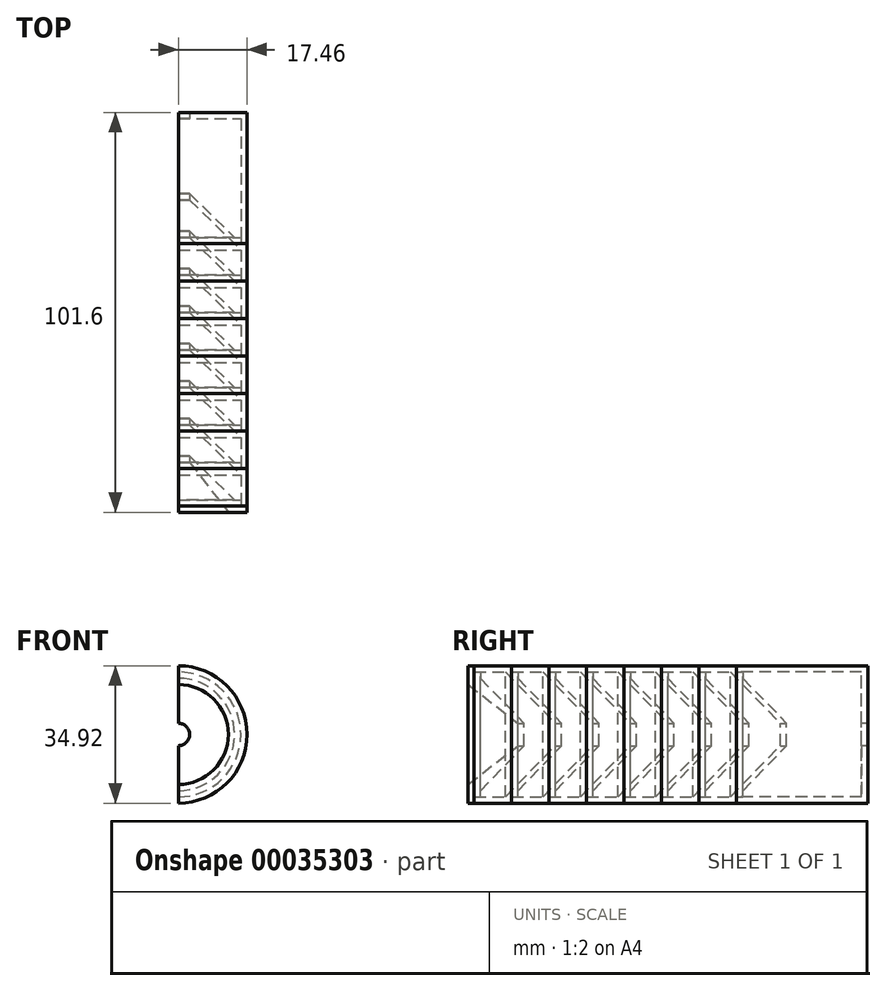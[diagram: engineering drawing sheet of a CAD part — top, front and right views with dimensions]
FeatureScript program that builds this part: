
annotation { "Feature Type Name" : "Feature", "Feature Type Description" : "" }
export const myFeature = defineFeature(function(context is Context, id is Id, definition is map)
    precondition{}
    {
        {
            var Q0;
            Q0=qCreatedBy(makeId("Right.planeOp"),FACE);
            var sketch = newSketch(context, id + "F0", { "sketchPlane" : qUnion([Q0])});
            skLineSegment(sketch, "E0", {"start": v(-16.6, 0) * mm, "end": v(16.6, 0) * mm, "construction": true});
            skLineSegment(sketch, "E1", {"start": v(-11.9, 15.88) * mm, "end": v(-11.9, 17.46) * mm});
            skLineSegment(sketch, "E2", {"start": v(-11.9, 17.46) * mm, "end": v(-21.43, 17.46) * mm});
            skLineSegment(sketch, "E3", {"start": v(-21.43, 17.46) * mm, "end": v(-21.43, 15.88) * mm});
            skLineSegment(sketch, "E4", {"start": v(-21.43, 15.88) * mm, "end": v(-13.5, 15.88) * mm});
            skLineSegment(sketch, "E5", {"start": v(-13.5, 15.88) * mm, "end": v(-0.8, 2.86) * mm});
            skLineSegment(sketch, "E6", {"start": v(-0.8, 2.86) * mm, "end": v(0.8, 2.86) * mm});
            skPoint(sketch, "E7", {"position": v(0, 2.86) * mm});
            skLineSegment(sketch, "E8.bottom", {"start": v(-11.9, 15.88) * mm, "end": v(-10.36, 15.88) * mm});
            skLineSegment(sketch, "E8.top", {"start": v(-11.9, 15.88) * mm, "end": v(-10.36, 15.88) * mm});
            skLineSegment(sketch, "E8.left", {"start": v(-11.9, 15.88) * mm, "end": v(-11.9, 15.88) * mm});
            skLineSegment(sketch, "E8.right", {"start": v(-10.36, 15.88) * mm, "end": v(-10.36, 15.88) * mm});
            skLineSegment(sketch, "E9.top", {"start": v(-10.36, 14.29) * mm, "end": v(-10.36, 14.29) * mm});
            skLineSegment(sketch, "E9.left", {"start": v(-10.36, 15.88) * mm, "end": v(-10.36, 14.29) * mm});
            skLineSegment(sketch, "E9.right", {"start": v(-10.36, 15.88) * mm, "end": v(-10.36, 14.29) * mm});
            skLineSegment(sketch, "E10", {"start": v(-10.36, 14.29) * mm, "end": v(0.8, 2.86) * mm});
            skSolve(sketch);
        }
        {
            var Q0;
            Q0=qCreatedBy(makeId("Right.planeOp"),FACE);
            var sketch = newSketch(context, id + "F1", { "sketchPlane" : qUnion([Q0])});
            skLineSegment(sketch, "E11", {"start": v(0, 0) * mm, "end": v(26.92, 0) * mm, "construction": true});
            skLineSegment(sketch, "E12", {"start": v(-2.38, 15.88) * mm, "end": v(-2.38, 17.46) * mm});
            skLineSegment(sketch, "E13", {"start": v(-2.38, 17.46) * mm, "end": v(-11.9, 17.46) * mm});
            skLineSegment(sketch, "E14", {"start": v(-11.9, 17.46) * mm, "end": v(-11.9, 15.88) * mm});
            skLineSegment(sketch, "E15", {"start": v(-11.9, 15.88) * mm, "end": v(-3.97, 15.88) * mm});
            skLineSegment(sketch, "E16", {"start": v(-3.97, 15.88) * mm, "end": v(8.73, 2.86) * mm});
            skLineSegment(sketch, "E17", {"start": v(8.73, 2.86) * mm, "end": v(10.32, 2.86) * mm});
            skPoint(sketch, "E18", {"position": v(9.52, 2.86) * mm});
            skLineSegment(sketch, "E19", {"start": v(-2.38, 15.88) * mm, "end": v(-0.83, 15.88) * mm});
            skLineSegment(sketch, "E20", {"start": v(-0.83, 15.88) * mm, "end": v(-0.83, 14.29) * mm});
            skLineSegment(sketch, "E21", {"start": v(-0.83, 14.29) * mm, "end": v(10.32, 2.86) * mm});
            skSolve(sketch);
        }
        {
            var Q0;
            Q0=qCreatedBy(makeId("Right.planeOp"),FACE);
            var sketch = newSketch(context, id + "F2", { "sketchPlane" : qUnion([Q0])});
            skLineSegment(sketch, "E22", {"start": v(-1.05, 0) * mm, "end": v(25.87, 0) * mm, "construction": true});
            skLineSegment(sketch, "E23", {"start": v(-21.43, 15.88) * mm, "end": v(-21.43, 17.46) * mm});
            skLineSegment(sketch, "E24", {"start": v(-21.43, 17.46) * mm, "end": v(-30.96, 17.46) * mm});
            skLineSegment(sketch, "E25", {"start": v(-30.96, 17.46) * mm, "end": v(-30.96, 15.88) * mm});
            skLineSegment(sketch, "E26", {"start": v(-30.96, 15.88) * mm, "end": v(-23.02, 15.88) * mm});
            skLineSegment(sketch, "E27", {"start": v(-23.02, 15.88) * mm, "end": v(-10.32, 2.86) * mm});
            skLineSegment(sketch, "E28", {"start": v(-10.32, 2.86) * mm, "end": v(-8.73, 2.86) * mm});
            skPoint(sketch, "E29", {"position": v(-9.53, 2.86) * mm});
            skLineSegment(sketch, "E30", {"start": v(-21.43, 15.88) * mm, "end": v(-19.88, 15.88) * mm});
            skLineSegment(sketch, "E31", {"start": v(-19.88, 15.88) * mm, "end": v(-19.88, 14.29) * mm});
            skLineSegment(sketch, "E32", {"start": v(-19.88, 14.29) * mm, "end": v(-8.73, 2.86) * mm});
            skSolve(sketch);
        }
        {
            var Q0;
            Q0=qCreatedBy(makeId("Right.planeOp"),FACE);
            var sketch = newSketch(context, id + "F3", { "sketchPlane" : qUnion([Q0])});
            skLineSegment(sketch, "E33", {"start": v(14.94, 0) * mm, "end": v(41.87, 0) * mm, "construction": true});
            skLineSegment(sketch, "E34", {"start": v(-30.96, 15.88) * mm, "end": v(-30.96, 17.46) * mm});
            skLineSegment(sketch, "E35", {"start": v(-30.96, 17.46) * mm, "end": v(-40.48, 17.46) * mm});
            skLineSegment(sketch, "E36", {"start": v(-40.48, 17.46) * mm, "end": v(-40.48, 15.88) * mm});
            skLineSegment(sketch, "E37", {"start": v(-40.48, 15.88) * mm, "end": v(-32.54, 15.88) * mm});
            skLineSegment(sketch, "E38", {"start": v(-32.54, 15.88) * mm, "end": v(-19.84, 2.86) * mm});
            skLineSegment(sketch, "E39", {"start": v(-19.84, 2.86) * mm, "end": v(-18.26, 2.86) * mm});
            skPoint(sketch, "E40", {"position": v(-19.05, 2.86) * mm});
            skLineSegment(sketch, "E41", {"start": v(-30.96, 15.88) * mm, "end": v(-29.4, 15.88) * mm});
            skLineSegment(sketch, "E42", {"start": v(-29.4, 15.88) * mm, "end": v(-29.4, 14.29) * mm});
            skLineSegment(sketch, "E43", {"start": v(-29.4, 14.29) * mm, "end": v(-18.26, 2.86) * mm});
            skSolve(sketch);
        }
        {
            var Q0;
            Q0=qCreatedBy(makeId("Right.planeOp"),FACE);
            var sketch = newSketch(context, id + "F4", { "sketchPlane" : qUnion([Q0])});
            skLineSegment(sketch, "E44", {"start": v(14.94, 0) * mm, "end": v(41.87, 0) * mm, "construction": true});
            skLineSegment(sketch, "E45", {"start": v(-40.48, 15.88) * mm, "end": v(-40.48, 17.46) * mm});
            skLineSegment(sketch, "E46", {"start": v(-40.48, 17.46) * mm, "end": v(-50, 17.46) * mm});
            skLineSegment(sketch, "E47", {"start": v(-50, 17.46) * mm, "end": v(-50, 15.88) * mm});
            skLineSegment(sketch, "E48", {"start": v(-50, 15.88) * mm, "end": v(-42.07, 15.88) * mm});
            skLineSegment(sketch, "E49", {"start": v(-42.07, 15.88) * mm, "end": v(-29.37, 2.86) * mm});
            skLineSegment(sketch, "E50", {"start": v(-29.37, 2.86) * mm, "end": v(-27.78, 2.86) * mm});
            skPoint(sketch, "E51", {"position": v(-28.58, 2.86) * mm});
            skLineSegment(sketch, "E52", {"start": v(-40.48, 15.88) * mm, "end": v(-38.93, 15.88) * mm});
            skLineSegment(sketch, "E53", {"start": v(-38.93, 15.88) * mm, "end": v(-38.93, 14.29) * mm});
            skLineSegment(sketch, "E54", {"start": v(-38.93, 14.29) * mm, "end": v(-27.78, 2.86) * mm});
            skSolve(sketch);
        }
        {
            var Q0;
            Q0=qCreatedBy(makeId("Right.planeOp"),FACE);
            var sketch = newSketch(context, id + "F5", { "sketchPlane" : qUnion([Q0])});
            skLineSegment(sketch, "E55", {"start": v(14.94, 0) * mm, "end": v(41.87, 0) * mm, "construction": true});
            skLineSegment(sketch, "E56", {"start": v(7.14, 15.88) * mm, "end": v(7.14, 17.46) * mm});
            skLineSegment(sketch, "E57", {"start": v(7.14, 17.46) * mm, "end": v(-2.38, 17.46) * mm});
            skLineSegment(sketch, "E58", {"start": v(-2.38, 17.46) * mm, "end": v(-2.38, 15.88) * mm});
            skLineSegment(sketch, "E59", {"start": v(-2.38, 15.88) * mm, "end": v(5.56, 15.88) * mm});
            skLineSegment(sketch, "E60", {"start": v(5.56, 15.88) * mm, "end": v(18.26, 2.86) * mm});
            skLineSegment(sketch, "E61", {"start": v(18.26, 2.86) * mm, "end": v(19.84, 2.86) * mm});
            skPoint(sketch, "E62", {"position": v(19.05, 2.86) * mm});
            skLineSegment(sketch, "E63", {"start": v(7.14, 15.88) * mm, "end": v(8.7, 15.88) * mm});
            skLineSegment(sketch, "E64", {"start": v(8.7, 15.88) * mm, "end": v(8.7, 14.29) * mm});
            skLineSegment(sketch, "E65", {"start": v(8.7, 14.29) * mm, "end": v(19.84, 2.86) * mm});
            skSolve(sketch);
        }
        {
            var Q0;
            Q0=qCreatedBy(makeId("Right.planeOp"),FACE);
            var sketch = newSketch(context, id + "F6", { "sketchPlane" : qUnion([Q0])});
            skLineSegment(sketch, "E66", {"start": v(14.94, 0) * mm, "end": v(41.87, 0) * mm, "construction": true});
            skLineSegment(sketch, "E67", {"start": v(-50, 15.88) * mm, "end": v(-50, 17.46) * mm});
            skLineSegment(sketch, "E68", {"start": v(-51.6, 12.7) * mm, "end": v(-38.9, 2.86) * mm});
            skLineSegment(sketch, "E69", {"start": v(-38.9, 2.86) * mm, "end": v(-37.3, 2.86) * mm});
            skPoint(sketch, "E70", {"position": v(-38.1, 2.86) * mm});
            skLineSegment(sketch, "E71", {"start": v(-51.6, 12.7) * mm, "end": v(-51.6, 17.46) * mm});
            skLineSegment(sketch, "E72", {"start": v(-51.6, 17.46) * mm, "end": v(-50, 17.46) * mm});
            skLineSegment(sketch, "E73", {"start": v(-50, 15.88) * mm, "end": v(-48.46, 15.88) * mm});
            skLineSegment(sketch, "E74", {"start": v(-48.46, 15.88) * mm, "end": v(-48.46, 14.29) * mm});
            skLineSegment(sketch, "E75", {"start": v(-48.46, 14.29) * mm, "end": v(-37.3, 2.86) * mm});
            skPoint(sketch, "E76", {"position": v(-51.6, 10.64) * mm});
            skLineSegment(sketch, "E77", {"start": v(-51.6, 11.43) * mm, "end": v(-51.6, 9.84) * mm, "construction": true});
            skSolve(sketch);
        }
        {
            var Q0;
            Q0=qCreatedBy(makeId("Right.planeOp"),FACE);
            var sketch = newSketch(context, id + "F7", { "sketchPlane" : qUnion([Q0])});
            skLineSegment(sketch, "E78", {"start": v(14.94, 0) * mm, "end": v(41.87, 0) * mm, "construction": true});
            skLineSegment(sketch, "E79", {"start": v(16.67, 15.88) * mm, "end": v(16.67, 17.46) * mm});
            skLineSegment(sketch, "E80", {"start": v(16.67, 17.46) * mm, "end": v(7.14, 17.46) * mm});
            skLineSegment(sketch, "E81", {"start": v(7.14, 17.46) * mm, "end": v(7.14, 15.88) * mm});
            skLineSegment(sketch, "E82", {"start": v(7.14, 15.88) * mm, "end": v(15.08, 15.88) * mm});
            skLineSegment(sketch, "E83", {"start": v(15.08, 15.88) * mm, "end": v(27.78, 2.86) * mm});
            skLineSegment(sketch, "E84", {"start": v(27.78, 2.86) * mm, "end": v(29.37, 2.86) * mm});
            skPoint(sketch, "E85", {"position": v(28.58, 2.86) * mm});
            skLineSegment(sketch, "E86", {"start": v(16.67, 15.88) * mm, "end": v(18.22, 15.88) * mm});
            skLineSegment(sketch, "E87", {"start": v(18.22, 15.88) * mm, "end": v(18.22, 14.29) * mm});
            skLineSegment(sketch, "E88", {"start": v(18.22, 14.29) * mm, "end": v(29.37, 2.86) * mm});
            skSolve(sketch);
        }
        {
            var Q0;
            Q0=qCreatedBy(makeId("Right.planeOp"),FACE);
            var sketch = newSketch(context, id + "F8", { "sketchPlane" : qUnion([Q0])});
            skLineSegment(sketch, "E89.bottom", {"start": v(16.67, 17.46) * mm, "end": v(50, 17.46) * mm});
            skLineSegment(sketch, "E89.left", {"start": v(16.67, 17.46) * mm, "end": v(16.67, 15.88) * mm});
            skLineSegment(sketch, "E90", {"start": v(50, 17.46) * mm, "end": v(50, 2.86) * mm});
            skLineSegment(sketch, "E91", {"start": v(50, 2.86) * mm, "end": v(48.42, 2.86) * mm});
            skLineSegment(sketch, "E92", {"start": v(48.42, 2.86) * mm, "end": v(48.42, 15.88) * mm});
            skLineSegment(sketch, "E93", {"start": v(48.42, 15.88) * mm, "end": v(16.67, 15.88) * mm});
            skSolve(sketch);
        }
        {
            var Q0;
            Q0=makeQuery(id+"F0.imprint","IMPRINT",FACE,{"disambiguationData":[TD([[makeQuery(id+"F0.imprint","IMPRINT",EDGE,{"derivedFrom":sQuery(id+"F0.wireOp",EDGE,"E1")}),1.0]])]});
            var Q1;
            Q1=makeQuery(id+"F1.imprint","IMPRINT",FACE,{"disambiguationData":[TD([[makeQuery(id+"F1.imprint","IMPRINT",EDGE,{"derivedFrom":sQuery(id+"F1.wireOp",EDGE,"E12")}),1.0]])]});
            var Q2;
            Q2=makeQuery(id+"F2.imprint","IMPRINT",FACE,{"disambiguationData":[TD([[makeQuery(id+"F2.imprint","IMPRINT",EDGE,{"derivedFrom":sQuery(id+"F2.wireOp",EDGE,"E23")}),1.0]])]});
            var Q3;
            Q3=makeQuery(id+"F3.imprint","IMPRINT",FACE,{"disambiguationData":[TD([[makeQuery(id+"F3.imprint","IMPRINT",EDGE,{"derivedFrom":sQuery(id+"F3.wireOp",EDGE,"E34")}),1.0]])]});
            var Q4;
            Q4=makeQuery(id+"F5.imprint","IMPRINT",FACE,{"disambiguationData":[TD([[makeQuery(id+"F5.imprint","IMPRINT",EDGE,{"derivedFrom":sQuery(id+"F5.wireOp",EDGE,"E56")}),1.0]])]});
            var Q5;
            Q5=makeQuery(id+"F6.imprint","IMPRINT",FACE,{"disambiguationData":[TD([[makeQuery(id+"F6.imprint","IMPRINT",EDGE,{"derivedFrom":sQuery(id+"F6.wireOp",EDGE,"E67")}),1.0]])]});
            var Q6;
            Q6=makeQuery(id+"F7.imprint","IMPRINT",FACE,{"disambiguationData":[TD([[makeQuery(id+"F7.imprint","IMPRINT",EDGE,{"derivedFrom":sQuery(id+"F7.wireOp",EDGE,"E79")}),1.0]])]});
            var Q7;
            Q7=makeQuery(id+"F4.imprint","IMPRINT",FACE,{"disambiguationData":[TD([[makeQuery(id+"F4.imprint","IMPRINT",EDGE,{"derivedFrom":sQuery(id+"F4.wireOp",EDGE,"E45")}),1.0]])]});
            var Q8;
            Q8=makeQuery(id+"F8.imprint","IMPRINT",FACE,{"disambiguationData":[TD([[makeQuery(id+"F8.imprint","IMPRINT",EDGE,{"derivedFrom":sQuery(id+"F8.wireOp",EDGE,"E89.bottom")}),-1.0]])]});
            var Q9;
            Q9=sQuery(id+"F0.wireOp",EDGE,"E0");
            revolve(context, id + "F9", {"entities" : qUnion([Q0, Q1, Q2, Q3, Q4, Q5, Q6, Q7, Q8]), "axis" : qUnion([Q9]), "revolveType" : RevolveType.ONE_DIRECTION, "angle" : 180 * degree});
        }
    });
